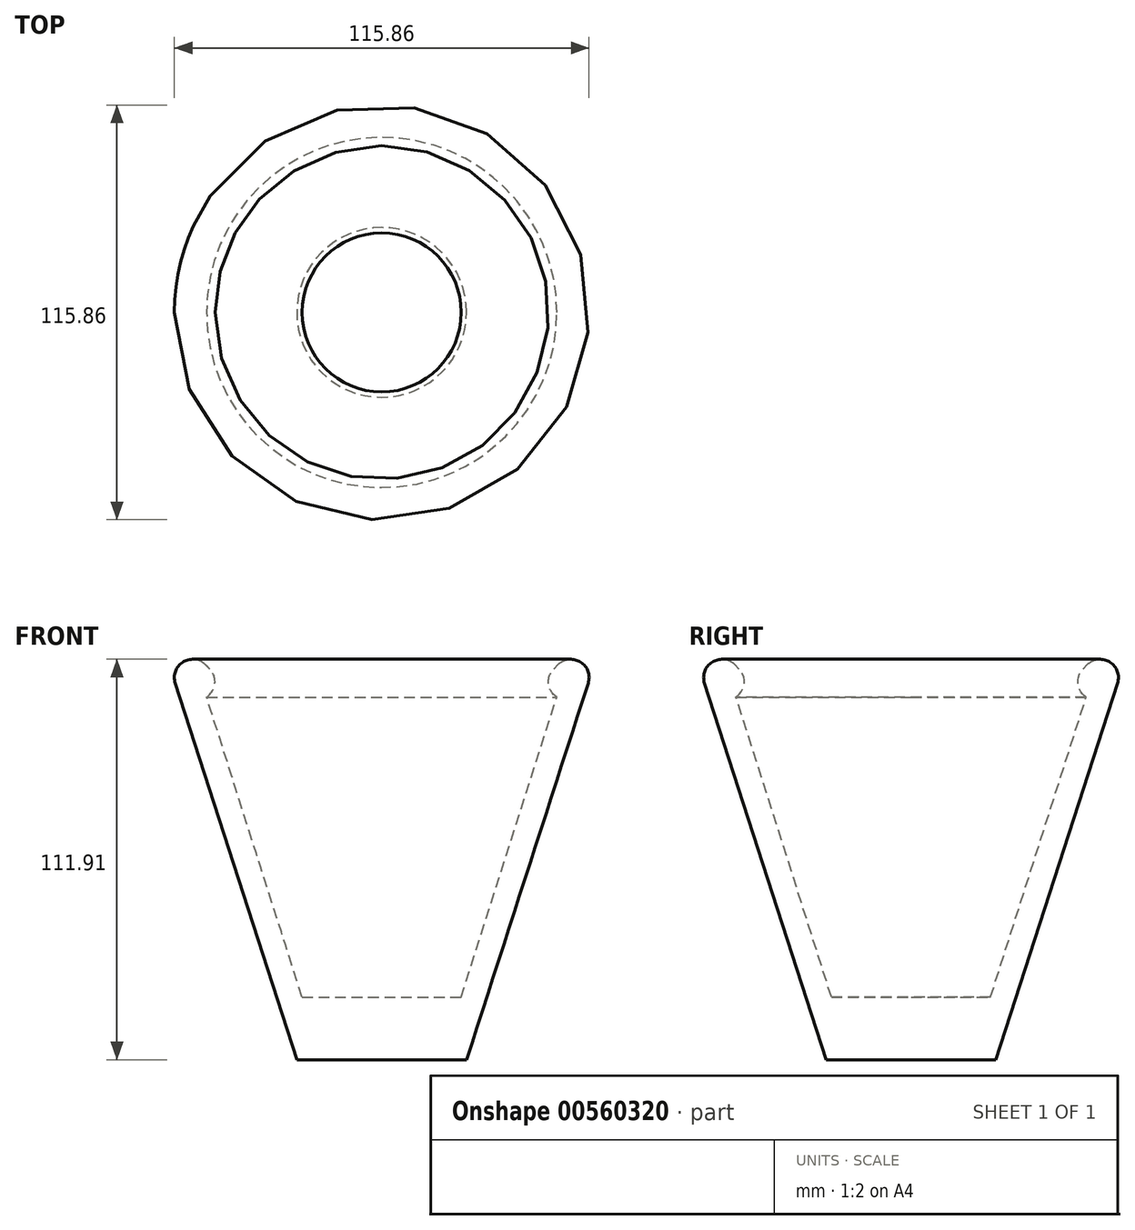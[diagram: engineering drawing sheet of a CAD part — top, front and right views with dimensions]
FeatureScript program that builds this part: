
annotation { "Feature Type Name" : "Feature", "Feature Type Description" : "" }
export const myFeature = defineFeature(function(context is Context, id is Id, definition is map)
    precondition{}
    {
        {
            var Q0;
            Q0=qCreatedBy(makeId("Right.planeOp"),FACE);
            var sketch = newSketch(context, id + "F0", { "sketchPlane" : qUnion([Q0])});
            skLineSegment(sketch, "E0", {"start": v(0, 38.32) * mm, "end": v(0, -51.55) * mm});
            skLineSegment(sketch, "E1", {"start": v(0, -51.55) * mm, "end": v(23.72, -51.55) * mm});
            skLineSegment(sketch, "E2", {"start": v(23.72, -51.55) * mm, "end": v(64.16, 73.77) * mm});
            skLineSegment(sketch, "E3", {"start": v(64.16, 73.77) * mm, "end": v(31.2, 40.81) * mm});
            skLineSegment(sketch, "E4", {"start": v(31.2, 40.81) * mm, "end": v(0, 38.32) * mm});
            skSolve(sketch);
        }
        {
            var Q0;
            Q0=makeQuery(id+"F0.imprint","IMPRINT",FACE,{"disambiguationData":[TD([[makeQuery(id+"F0.imprint","IMPRINT",EDGE,{"derivedFrom":sQuery(id+"F0.wireOp",EDGE,"E0")}),1.0]])]});
            var Q1;
            Q1=sQuery(id+"F0.wireOp",EDGE,"E0");
            revolve(context, id + "F1", {"entities" : qUnion([Q0]), "axis" : qUnion([Q1]), "revolveType" : RevolveType.FULL});
        }
        {
            var Q0;
            Q0=makeQuery(id+"F1.opRevolve","SWEPT_EDGE",EDGE,{"disambiguationData":[OSD([sQuery(id+"F0.wireOp",EDGE,"E2"),sQuery(id+"F0.wireOp",EDGE,"E3")])]});
            fillet(context, id + "F2", {"entities" : qUnion([Q0]), "radius" : 5.08 * mm, "tangentPropagation" : true, "allowEdgeOverflow" : false});
        }
        {
            var Q0;
            Q0=qCreatedBy(makeId("Front.planeOp"),FACE);
            var sketch = newSketch(context, id + "F3", { "sketchPlane" : qUnion([Q0])});
            skLineSegment(sketch, "E5", {"start": v(0, 49.8) * mm, "end": v(0, -34.08) * mm});
            skLineSegment(sketch, "E6", {"start": v(0, -34.08) * mm, "end": v(22.22, -34.08) * mm});
            skLineSegment(sketch, "E7", {"start": v(22.22, -34.08) * mm, "end": v(48.93, 49.8) * mm});
            skLineSegment(sketch, "E8", {"start": v(48.93, 49.8) * mm, "end": v(0, 49.8) * mm});
            skSolve(sketch);
        }
        {
            var Q0;
            Q0=makeQuery(id+"F3.imprint","IMPRINT",FACE,{"disambiguationData":[TD([[makeQuery(id+"F3.imprint","IMPRINT",EDGE,{"derivedFrom":sQuery(id+"F3.wireOp",EDGE,"E5")}),1.0]])]});
            var Q1;
            Q1=sQuery(id+"F3.wireOp",EDGE,"E5");
            revolve(context, id + "F4", {"operationType" : NewBodyOperationType.REMOVE, "entities" : qUnion([Q0]), "axis" : qUnion([Q1]), "revolveType" : RevolveType.FULL, "oppositeDirection" : true});
        }
        {
            var Q0;
            Q0=makeQuery(id+"F4.boolean.opBoolean","INTERSECT",EDGE,{"derivedFrom":[makeQuery(id+"F1.opRevolve","SWEPT_FACE",FACE,{"disambiguationData":[OSD([sQuery(id+"F0.wireOp",EDGE,"E3")])]}),makeQuery(id+"F4.opRevolve","SWEPT_FACE",FACE,{"disambiguationData":[OSD([sQuery(id+"F3.wireOp",EDGE,"E8")])]})]});
            fillet(context, id + "F5", {"entities" : qUnion([Q0]), "radius" : 5.08 * mm, "tangentPropagation" : true, "allowEdgeOverflow" : false});
        }
        {
            var Q0;
            Q0=qCreatedBy(makeId("Front.planeOp"),FACE);
            var sketch = newSketch(context, id + "F6", { "sketchPlane" : qUnion([Q0])});
            skLineSegment(sketch, "E9", {"start": v(44.19, 39.07) * mm, "end": v(66.65, 44.8) * mm});
            skLineSegment(sketch, "E10", {"start": v(66.65, 44.8) * mm, "end": v(48.43, -25.84) * mm});
            skLineSegment(sketch, "E11", {"start": v(48.43, -25.84) * mm, "end": v(18.97, -37.07) * mm});
            skSolve(sketch);
        }
    });
